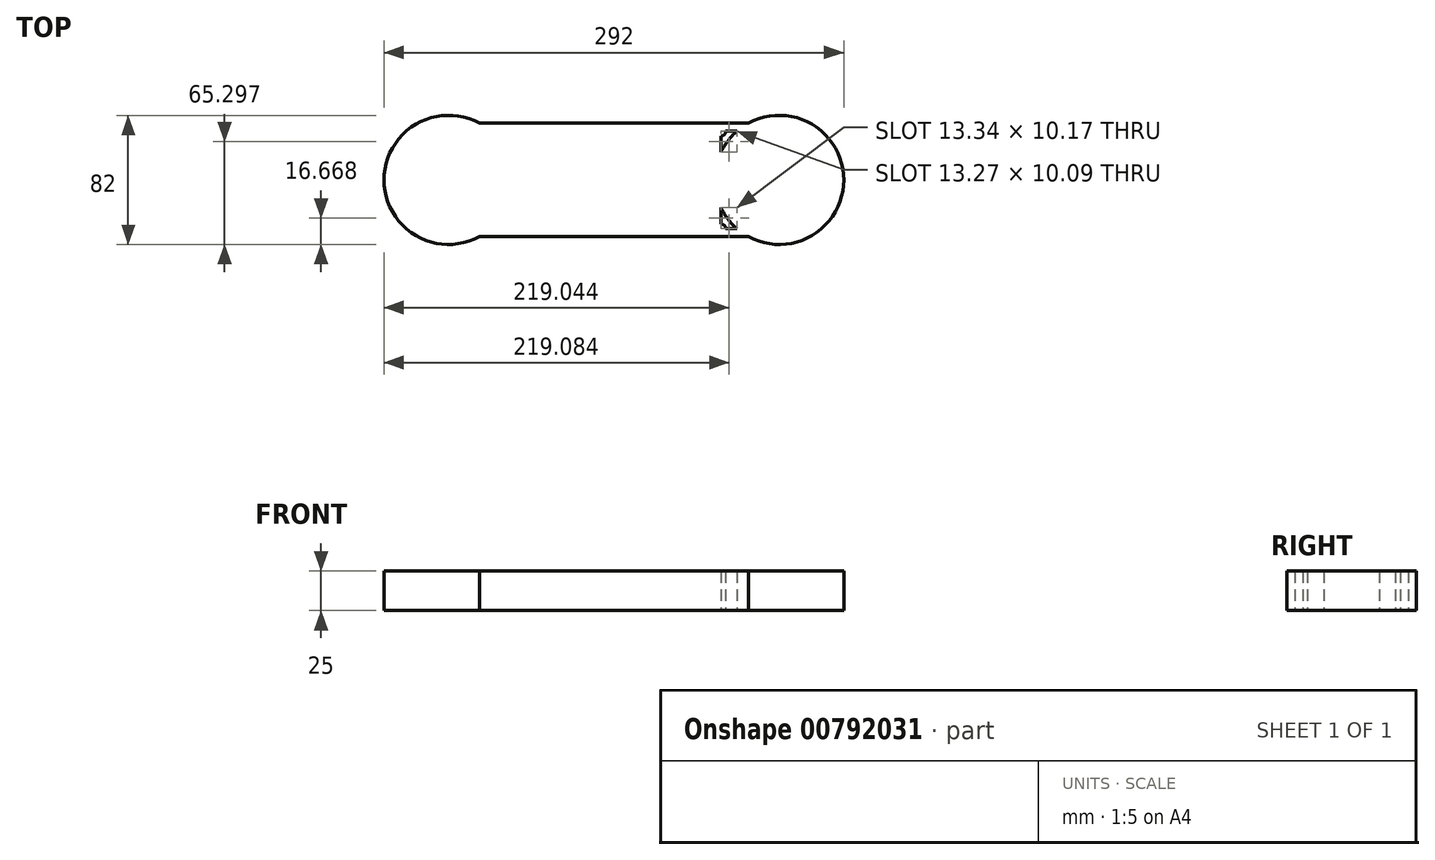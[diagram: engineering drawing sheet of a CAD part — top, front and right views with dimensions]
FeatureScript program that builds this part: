
annotation { "Feature Type Name" : "Feature", "Feature Type Description" : "" }
export const myFeature = defineFeature(function(context is Context, id is Id, definition is map)
    precondition{}
    {
        {
            var Q0;
            Q0=qCreatedBy(makeId("Top.planeOp"),FACE);
            var sketch = newSketch(context, id + "F0", { "sketchPlane" : qUnion([Q0])});
            skCircle(sketch, "E0", {"center": v(0, 0) * mm, "radius": 36 * mm});
            skCircle(sketch, "E1", {"center": v(210, 0) * mm, "radius": 36 * mm});
            skLineSegment(sketch, "E2", {"start": v(0, 36) * mm, "end": v(210, 36) * mm});
            skLineSegment(sketch, "E3", {"start": v(210, -36) * mm, "end": v(0, -36) * mm});
            skCircle(sketch, "E4", {"center": v(0, 0) * mm, "radius": 6.6 * mm});
            skCircle(sketch, "E5", {"center": v(0, 0) * mm, "radius": 10 * mm});
            skCircle(sketch, "E6", {"center": v(0, 0) * mm, "radius": 30 * mm});
            skCircle(sketch, "E7", {"center": v(210, 0) * mm, "radius": 30 * mm});
            skCircle(sketch, "E8", {"center": v(210, 0) * mm, "radius": 18.75 * mm});
            skCircle(sketch, "E9", {"center": v(210, 0) * mm, "radius": 21.5 * mm});
            skLineSegment(sketch, "E10", {"start": v(18.42, 30.93) * mm, "end": v(191.58, 30.93) * mm});
            skLineSegment(sketch, "E11", {"start": v(18.3, -31) * mm, "end": v(191.7, -31) * mm});
            skLineSegment(sketch, "E12", {"start": v(165, 30.93) * mm, "end": v(165, -31) * mm});
            skLineSegment(sketch, "E13", {"start": v(45, 30.93) * mm, "end": v(45, -31) * mm});
            skCircle(sketch, "E14", {"center": v(210, 0) * mm, "radius": 41 * mm});
            skCircle(sketch, "E15", {"center": v(0, 0) * mm, "radius": 41 * mm});
            skLineSegment(sketch, "E16.bottom", {"start": v(37, 30.93) * mm, "end": v(173, 30.93) * mm});
            skLineSegment(sketch, "E16.top", {"start": v(37, -31) * mm, "end": v(173, -31) * mm});
            skLineSegment(sketch, "E16.left", {"start": v(37, 30.93) * mm, "end": v(37, -31) * mm});
            skLineSegment(sketch, "E16.right", {"start": v(173, 30.93) * mm, "end": v(173, -31) * mm});
            skCircle(sketch, "E17", {"center": v(37, 30.93) * mm, "radius": 3 * mm});
            skCircle(sketch, "E18", {"center": v(37, -31) * mm, "radius": 3 * mm});
            skCircle(sketch, "E19", {"center": v(173, 30.93) * mm, "radius": 3 * mm});
            skCircle(sketch, "E20", {"center": v(173, -31) * mm, "radius": 3 * mm});
            skLineSegment(sketch, "E21", {"start": v(-32, -16.5) * mm, "end": v(-32, 16.5) * mm});
            skLineSegment(sketch, "E22", {"start": v(242, -16.5) * mm, "end": v(242, 16.5) * mm});
            skSolve(sketch);
        }
        {
            var Q0;
            {var subQ1=sQuery(id+"F0.wireOp",EDGE,"E16.top");var subQ3=sQuery(id+"F0.wireOp",EDGE,"E20");var subQ4=makeQuery(id+"F0.imprint","INTERSECT",VERTEX,{"derivedFrom":[subQ1,subQ3]});Q0=makeQuery(id+"F0.imprint","IMPRINT",FACE,{"disambiguationData":[TD([[makeQuery(id+"F0.imprint","IMPRINT",EDGE,{"disambiguationData":[TD([[subQ4,1.0]])],"derivedFrom":subQ3}),1.0]])]});}
            var Q1;
            {var subQ1=sQuery(id+"F0.wireOp",EDGE,"E12");Q1=makeQuery(id+"F0.imprint","IMPRINT",FACE,{"disambiguationData":[TD([[makeQuery(id+"F0.imprint","IMPRINT",EDGE,{"derivedFrom":subQ1}),1.0]])]});}
            var Q2;
            {var subQ0=sQuery(id+"F0.wireOp",EDGE,"E15");var subQ1=sQuery(id+"F0.wireOp",EDGE,"E11");var subQ2=makeQuery(id+"F0.imprint","INTERSECT",VERTEX,{"derivedFrom":[subQ1,subQ0]});Q2=makeQuery(id+"F0.imprint","IMPRINT",FACE,{"disambiguationData":[TD([[makeQuery(id+"F0.imprint","IMPRINT",EDGE,{"disambiguationData":[TD([[subQ2,-1.0]])],"derivedFrom":subQ1}),1.0]])]});}
            var Q3;
            {var subQ1=sQuery(id+"F0.wireOp",EDGE,"E16.bottom");var subQ3=sQuery(id+"F0.wireOp",EDGE,"E19");var subQ4=makeQuery(id+"F0.imprint","INTERSECT",VERTEX,{"derivedFrom":[subQ1,subQ3]});Q3=makeQuery(id+"F0.imprint","IMPRINT",FACE,{"disambiguationData":[TD([[makeQuery(id+"F0.imprint","IMPRINT",EDGE,{"disambiguationData":[TD([[subQ4,-1.0]])],"derivedFrom":subQ3}),1.0]])]});}
            var Q4;
            Q4=makeQuery(id+"F0.imprint","IMPRINT",FACE,{"disambiguationData":[TD([[makeQuery(id+"F0.imprint","IMPRINT",EDGE,{"derivedFrom":sQuery(id+"F0.wireOp",EDGE,"E7")}),-1.0]])]});
            var Q5;
            {var subQ1=sQuery(id+"F0.wireOp",EDGE,"E11");var subQ3=sQuery(id+"F0.wireOp",EDGE,"E20");var subQ4=makeQuery(id+"F0.imprint","INTERSECT",VERTEX,{"derivedFrom":[subQ1,subQ3]});Q5=makeQuery(id+"F0.imprint","IMPRINT",FACE,{"disambiguationData":[TD([[makeQuery(id+"F0.imprint","IMPRINT",EDGE,{"disambiguationData":[TD([[subQ4,-1.0]])],"derivedFrom":subQ3}),1.0]])]});}
            var Q6;
            Q6=makeQuery(id+"F0.imprint","IMPRINT",FACE,{"disambiguationData":[TD([[makeQuery(id+"F0.imprint","IMPRINT",EDGE,{"derivedFrom":sQuery(id+"F0.wireOp",EDGE,"E6")}),-1.0]])]});
            var Q7;
            {var subQ0=sQuery(id+"F0.wireOp",EDGE,"E15");var subQ1=sQuery(id+"F0.wireOp",EDGE,"E10");var subQ2=makeQuery(id+"F0.imprint","INTERSECT",VERTEX,{"derivedFrom":[subQ1,subQ0]});Q7=makeQuery(id+"F0.imprint","IMPRINT",FACE,{"disambiguationData":[TD([[makeQuery(id+"F0.imprint","IMPRINT",EDGE,{"disambiguationData":[TD([[subQ2,-1.0]])],"derivedFrom":subQ1}),-1.0]])]});}
            var Q8;
            {var subQ0=sQuery(id+"F0.wireOp",EDGE,"E2");var subQ1=sQuery(id+"F0.wireOp",EDGE,"E1");var subQ2=makeQuery(id+"F0.imprint","INTERSECT",VERTEX,{"derivedFrom":[subQ1,subQ0]});Q8=makeQuery(id+"F0.imprint","IMPRINT",FACE,{"disambiguationData":[TD([[makeQuery(id+"F0.imprint","IMPRINT",EDGE,{"disambiguationData":[TD([[subQ2,-1.0]])],"derivedFrom":subQ1}),-1.0]])]});}
            var Q9;
            {var subQ0=sQuery(id+"F0.wireOp",EDGE,"E14");var subQ1=sQuery(id+"F0.wireOp",EDGE,"E3");var subQ2=makeQuery(id+"F0.imprint","INTERSECT",VERTEX,{"derivedFrom":[subQ1,subQ0]});Q9=makeQuery(id+"F0.imprint","IMPRINT",FACE,{"disambiguationData":[TD([[makeQuery(id+"F0.imprint","IMPRINT",EDGE,{"disambiguationData":[TD([[subQ2,-1.0]])],"derivedFrom":subQ1}),-1.0]])]});}
            var Q10;
            {var subQ0=sQuery(id+"F0.wireOp",EDGE,"E3");var subQ1=sQuery(id+"F0.wireOp",EDGE,"E0");var subQ2=makeQuery(id+"F0.imprint","INTERSECT",VERTEX,{"derivedFrom":[subQ1,subQ0]});Q10=makeQuery(id+"F0.imprint","IMPRINT",FACE,{"disambiguationData":[TD([[makeQuery(id+"F0.imprint","IMPRINT",EDGE,{"disambiguationData":[TD([[subQ2,-1.0]])],"derivedFrom":subQ1}),-1.0]])]});}
            var Q11;
            {var subQ1=sQuery(id+"F0.wireOp",EDGE,"E13");Q11=makeQuery(id+"F0.imprint","IMPRINT",FACE,{"disambiguationData":[TD([[makeQuery(id+"F0.imprint","IMPRINT",EDGE,{"derivedFrom":subQ1}),-1.0]])]});}
            var Q12;
            {var subQ0=sQuery(id+"F0.wireOp",EDGE,"E2");var subQ1=sQuery(id+"F0.wireOp",EDGE,"E0");var subQ2=makeQuery(id+"F0.imprint","INTERSECT",VERTEX,{"derivedFrom":[subQ1,subQ0]});Q12=makeQuery(id+"F0.imprint","IMPRINT",FACE,{"disambiguationData":[TD([[makeQuery(id+"F0.imprint","IMPRINT",EDGE,{"disambiguationData":[TD([[subQ2,1.0]])],"derivedFrom":subQ1}),-1.0]])]});}
            var Q13;
            {var subQ1=sQuery(id+"F0.wireOp",EDGE,"E16.top");var subQ3=sQuery(id+"F0.wireOp",EDGE,"E18");var subQ4=makeQuery(id+"F0.imprint","INTERSECT",VERTEX,{"derivedFrom":[subQ1,subQ3]});Q13=makeQuery(id+"F0.imprint","IMPRINT",FACE,{"disambiguationData":[TD([[makeQuery(id+"F0.imprint","IMPRINT",EDGE,{"disambiguationData":[TD([[subQ4,-1.0]])],"derivedFrom":subQ3}),1.0]])]});}
            var Q14;
            {var subQ0=sQuery(id+"F0.wireOp",EDGE,"E19");var subQ1=sQuery(id+"F0.wireOp",EDGE,"E10");var subQ2=makeQuery(id+"F0.imprint","INTERSECT",VERTEX,{"derivedFrom":[subQ1,subQ0]});Q14=makeQuery(id+"F0.imprint","IMPRINT",FACE,{"disambiguationData":[TD([[makeQuery(id+"F0.imprint","IMPRINT",EDGE,{"disambiguationData":[TD([[subQ2,-1.0]])],"derivedFrom":subQ1}),-1.0]])]});}
            var Q15;
            {var subQ1=sQuery(id+"F0.wireOp",EDGE,"E1");var subQ5=sQuery(id+"F0.wireOp",EDGE,"E10");var subQ9=makeQuery(id+"F0.imprint","INTERSECT",VERTEX,{"derivedFrom":[subQ1,subQ5]});Q15=makeQuery(id+"F0.imprint","IMPRINT",FACE,{"disambiguationData":[TD([[makeQuery(id+"F0.imprint","IMPRINT",EDGE,{"disambiguationData":[TD([[subQ9,-1.0]])],"derivedFrom":subQ1}),-1.0]])]});}
            var Q16;
            {var subQ1=sQuery(id+"F0.wireOp",EDGE,"E11");var subQ3=sQuery(id+"F0.wireOp",EDGE,"E18");var subQ4=makeQuery(id+"F0.imprint","INTERSECT",VERTEX,{"derivedFrom":[subQ1,subQ3]});Q16=makeQuery(id+"F0.imprint","IMPRINT",FACE,{"disambiguationData":[TD([[makeQuery(id+"F0.imprint","IMPRINT",EDGE,{"disambiguationData":[TD([[subQ4,1.0]])],"derivedFrom":subQ3}),1.0]])]});}
            var Q17;
            {var subQ1=sQuery(id+"F0.wireOp",EDGE,"E16.bottom");var subQ3=sQuery(id+"F0.wireOp",EDGE,"E17");var subQ4=makeQuery(id+"F0.imprint","INTERSECT",VERTEX,{"derivedFrom":[subQ1,subQ3]});Q17=makeQuery(id+"F0.imprint","IMPRINT",FACE,{"disambiguationData":[TD([[makeQuery(id+"F0.imprint","IMPRINT",EDGE,{"disambiguationData":[TD([[subQ4,1.0]])],"derivedFrom":subQ3}),1.0]])]});}
            var Q18;
            {var subQ1=sQuery(id+"F0.wireOp",EDGE,"E10");var subQ3=sQuery(id+"F0.wireOp",EDGE,"E19");var subQ4=makeQuery(id+"F0.imprint","INTERSECT",VERTEX,{"derivedFrom":[subQ1,subQ3]});Q18=makeQuery(id+"F0.imprint","IMPRINT",FACE,{"disambiguationData":[TD([[makeQuery(id+"F0.imprint","IMPRINT",EDGE,{"disambiguationData":[TD([[subQ4,1.0]])],"derivedFrom":subQ3}),1.0]])]});}
            var Q19;
            {var subQ1=sQuery(id+"F0.wireOp",EDGE,"E10");var subQ5=sQuery(id+"F0.wireOp",EDGE,"E0");var subQ6=makeQuery(id+"F0.imprint","INTERSECT",VERTEX,{"derivedFrom":[subQ5,subQ1]});Q19=makeQuery(id+"F0.imprint","IMPRINT",FACE,{"disambiguationData":[TD([[makeQuery(id+"F0.imprint","IMPRINT",EDGE,{"disambiguationData":[TD([[subQ6,1.0]])],"derivedFrom":subQ5}),-1.0]])]});}
            var Q20;
            {var subQ1=sQuery(id+"F0.wireOp",EDGE,"E11");var subQ3=sQuery(id+"F0.wireOp",EDGE,"E18");var subQ4=makeQuery(id+"F0.imprint","INTERSECT",VERTEX,{"derivedFrom":[subQ1,subQ3]});Q20=makeQuery(id+"F0.imprint","IMPRINT",FACE,{"disambiguationData":[TD([[makeQuery(id+"F0.imprint","IMPRINT",EDGE,{"disambiguationData":[TD([[subQ4,-1.0]])],"derivedFrom":subQ3}),1.0]])]});}
            var Q21;
            {var subQ1=sQuery(id+"F0.wireOp",EDGE,"E11");var subQ3=sQuery(id+"F0.wireOp",EDGE,"E20");var subQ4=makeQuery(id+"F0.imprint","INTERSECT",VERTEX,{"derivedFrom":[subQ1,subQ3]});Q21=makeQuery(id+"F0.imprint","IMPRINT",FACE,{"disambiguationData":[TD([[makeQuery(id+"F0.imprint","IMPRINT",EDGE,{"disambiguationData":[TD([[subQ4,1.0]])],"derivedFrom":subQ3}),1.0]])]});}
            var Q22;
            {var subQ0=sQuery(id+"F0.wireOp",EDGE,"E12");Q22=makeQuery(id+"F0.imprint","IMPRINT",FACE,{"disambiguationData":[TD([[makeQuery(id+"F0.imprint","IMPRINT",EDGE,{"derivedFrom":subQ0}),-1.0]])]});}
            var Q23;
            Q23=makeQuery(id+"F0.imprint","IMPRINT",FACE,{"disambiguationData":[TD([[makeQuery(id+"F0.imprint","IMPRINT",EDGE,{"derivedFrom":sQuery(id+"F0.wireOp",EDGE,"E4")}),1.0]])]});
            var Q24;
            Q24=makeQuery(id+"F0.imprint","IMPRINT",FACE,{"disambiguationData":[TD([[makeQuery(id+"F0.imprint","IMPRINT",EDGE,{"derivedFrom":sQuery(id+"F0.wireOp",EDGE,"E8")}),1.0]])]});
            var Q25;
            {var subQ0=sQuery(id+"F0.wireOp",EDGE,"E21");Q25=makeQuery(id+"F0.imprint","IMPRINT",FACE,{"disambiguationData":[TD([[makeQuery(id+"F0.imprint","IMPRINT",EDGE,{"derivedFrom":subQ0}),1.0]])]});}
            var Q26;
            {var subQ0=sQuery(id+"F0.wireOp",EDGE,"E22");Q26=makeQuery(id+"F0.imprint","IMPRINT",FACE,{"disambiguationData":[TD([[makeQuery(id+"F0.imprint","IMPRINT",EDGE,{"derivedFrom":subQ0}),-1.0]])]});}
            var Q27;
            Q27=makeQuery(id+"F0.imprint","IMPRINT",FACE,{"disambiguationData":[TD([[makeQuery(id+"F0.imprint","IMPRINT",EDGE,{"derivedFrom":sQuery(id+"F0.wireOp",EDGE,"E4")}),-1.0]])]});
            var Q28;
            Q28=makeQuery(id+"F0.imprint","IMPRINT",FACE,{"disambiguationData":[TD([[makeQuery(id+"F0.imprint","IMPRINT",EDGE,{"derivedFrom":sQuery(id+"F0.wireOp",EDGE,"E5")}),-1.0]])]});
            var Q29;
            Q29=makeQuery(id+"F0.imprint","IMPRINT",FACE,{"disambiguationData":[TD([[makeQuery(id+"F0.imprint","IMPRINT",EDGE,{"derivedFrom":sQuery(id+"F0.wireOp",EDGE,"E7")}),1.0]])]});
            var Q30;
            Q30=makeQuery(id+"F0.imprint","IMPRINT",FACE,{"disambiguationData":[TD([[makeQuery(id+"F0.imprint","IMPRINT",EDGE,{"derivedFrom":sQuery(id+"F0.wireOp",EDGE,"E8")}),-1.0]])]});
            var Q31;
            {var subQ0=sQuery(id+"F0.wireOp",EDGE,"E16.right");var subQ1=sQuery(id+"F0.wireOp",EDGE,"E14");var subQ2=makeQuery(id+"F0.imprint","INTERSECT",VERTEX,{"disambiguationData":[OD(0.0)],"derivedFrom":[subQ1,subQ0]});Q31=makeQuery(id+"F0.imprint","IMPRINT",FACE,{"disambiguationData":[TD([[makeQuery(id+"F0.imprint","IMPRINT",EDGE,{"disambiguationData":[TD([[subQ2,-1.0]])],"derivedFrom":subQ1}),1.0]])]});}
            var Q32;
            {var subQ0=sQuery(id+"F0.wireOp",EDGE,"E16.left");var subQ1=sQuery(id+"F0.wireOp",EDGE,"E15");var subQ2=makeQuery(id+"F0.imprint","INTERSECT",VERTEX,{"disambiguationData":[OD(0.0)],"derivedFrom":[subQ1,subQ0]});Q32=makeQuery(id+"F0.imprint","IMPRINT",FACE,{"disambiguationData":[TD([[makeQuery(id+"F0.imprint","IMPRINT",EDGE,{"disambiguationData":[TD([[subQ2,1.0]])],"derivedFrom":subQ1}),1.0]])]});}
            var Q33;
            {var subQ1=sQuery(id+"F0.wireOp",EDGE,"E10");var subQ3=sQuery(id+"F0.wireOp",EDGE,"E17");var subQ4=makeQuery(id+"F0.imprint","INTERSECT",VERTEX,{"derivedFrom":[subQ1,subQ3]});Q33=makeQuery(id+"F0.imprint","IMPRINT",FACE,{"disambiguationData":[TD([[makeQuery(id+"F0.imprint","IMPRINT",EDGE,{"disambiguationData":[TD([[subQ4,1.0]])],"derivedFrom":subQ3}),1.0]])]});}
            var Q34;
            {var subQ1=sQuery(id+"F0.wireOp",EDGE,"E10");var subQ3=sQuery(id+"F0.wireOp",EDGE,"E17");var subQ4=makeQuery(id+"F0.imprint","INTERSECT",VERTEX,{"derivedFrom":[subQ1,subQ3]});Q34=makeQuery(id+"F0.imprint","IMPRINT",FACE,{"disambiguationData":[TD([[makeQuery(id+"F0.imprint","IMPRINT",EDGE,{"disambiguationData":[TD([[subQ4,-1.0]])],"derivedFrom":subQ3}),1.0]])]});}
            var Q35;
            {var subQ1=sQuery(id+"F0.wireOp",EDGE,"E10");var subQ3=sQuery(id+"F0.wireOp",EDGE,"E19");var subQ4=makeQuery(id+"F0.imprint","INTERSECT",VERTEX,{"derivedFrom":[subQ1,subQ3]});Q35=makeQuery(id+"F0.imprint","IMPRINT",FACE,{"disambiguationData":[TD([[makeQuery(id+"F0.imprint","IMPRINT",EDGE,{"disambiguationData":[TD([[subQ4,-1.0]])],"derivedFrom":subQ3}),1.0]])]});}
            var Q36;
            {var subQ0=sQuery(id+"F0.wireOp",EDGE,"E3");var subQ1=sQuery(id+"F0.wireOp",EDGE,"E1");var subQ2=makeQuery(id+"F0.imprint","INTERSECT",VERTEX,{"derivedFrom":[subQ1,subQ0]});Q36=makeQuery(id+"F0.imprint","IMPRINT",FACE,{"disambiguationData":[TD([[makeQuery(id+"F0.imprint","IMPRINT",EDGE,{"disambiguationData":[TD([[subQ2,1.0]])],"derivedFrom":subQ1}),-1.0]])]});}
            var Q37;
            {var subQ0=sQuery(id+"F0.wireOp",EDGE,"E20");var subQ1=sQuery(id+"F0.wireOp",EDGE,"E11");var subQ2=makeQuery(id+"F0.imprint","INTERSECT",VERTEX,{"derivedFrom":[subQ1,subQ0]});Q37=makeQuery(id+"F0.imprint","IMPRINT",FACE,{"disambiguationData":[TD([[makeQuery(id+"F0.imprint","IMPRINT",EDGE,{"disambiguationData":[TD([[subQ2,-1.0]])],"derivedFrom":subQ1}),1.0]])]});}
            var Q38;
            {var subQ0=sQuery(id+"F0.wireOp",EDGE,"E2");var subQ1=sQuery(id+"F0.wireOp",EDGE,"E1");var subQ2=makeQuery(id+"F0.imprint","INTERSECT",VERTEX,{"derivedFrom":[subQ1,subQ0]});Q38=makeQuery(id+"F0.imprint","IMPRINT",FACE,{"disambiguationData":[TD([[makeQuery(id+"F0.imprint","IMPRINT",EDGE,{"disambiguationData":[TD([[subQ2,1.0]])],"derivedFrom":subQ1}),-1.0]])]});}
            var Q39;
            {var subQ0=sQuery(id+"F0.wireOp",EDGE,"E15");var subQ6=sQuery(id+"F0.wireOp",EDGE,"E2");var subQ11=makeQuery(id+"F0.imprint","INTERSECT",VERTEX,{"derivedFrom":[subQ6,subQ0]});Q39=makeQuery(id+"F0.imprint","IMPRINT",FACE,{"disambiguationData":[TD([[makeQuery(id+"F0.imprint","IMPRINT",EDGE,{"disambiguationData":[TD([[subQ11,-1.0]])],"derivedFrom":subQ6}),-1.0]])]});}
            var Q40;
            {var subQ1=sQuery(id+"F0.wireOp",EDGE,"E0");var subQ5=sQuery(id+"F0.wireOp",EDGE,"E2");var subQ6=makeQuery(id+"F0.imprint","INTERSECT",VERTEX,{"derivedFrom":[subQ1,subQ5]});Q40=makeQuery(id+"F0.imprint","IMPRINT",FACE,{"disambiguationData":[TD([[makeQuery(id+"F0.imprint","IMPRINT",EDGE,{"disambiguationData":[TD([[subQ6,-1.0]])],"derivedFrom":subQ1}),-1.0]])]});}
            extrude(context, id + "F1", {"entities" : qUnion([Q0, Q1, Q2, Q3, Q4, Q5, Q6, Q7, Q8, Q9, Q10, Q11, Q12, Q13, Q14, Q15, Q16, Q17, Q18, Q19, Q20, Q21, Q22, Q23, Q24, Q25, Q26, Q27, Q28, Q29, Q30, Q31, Q32, Q33, Q34, Q35, Q36, Q37, Q38, Q39, Q40]), "depth" : 25 * mm, "offsetDistance" : 25 * mm});
        }
    });
